# Revit family: SU-420-G_GENERADO
name_source: partatom
category: Equipos mecánicos
revit_build: Autodesk Revit 2014 (Build: 20130308_1515(x64)
units: mm (PartAtom-declared; Revit-internal decimal feet)

## types (14) — shared parameters
Depth = 529 mm  [stored 1.73556 ft]
Fabricante = SAMMIC S.L.
Foodservice Equipment Identifier = Sí
Height = 448 mm  [stored 1.46982 ft]
Revision Code = 1
URL = https://www.sammic.com
URL Cutsheet = http://www.sammic.com
Width = 484 mm  [stored 1.58793 ft]

## per-type parameters (varying)
| type | Comentarios de tipo | Cycle | FL Amps | Modelo | Specification by Manufacturer | Volts | Weight in Pounds |
| Vacuum packing machine SU-416G 230/50-60/1 | Tabletop model. 16 m³/h. 420 mm. | 50 Hz | 4 A | 1140761 | 420 mm. sealing bar.
16 m³/h Busch vacuum pump.
Vacuum controlled by sensor. | 230 V | 143.3 |
| Vacuum packing machine SU-416GP 230/50-60/1 | Tabletop model. 16 m³/h. 420 mm. | 50 Hz | 4 A | 1140763 | 420 mm. sealing bar.
16 m³/h Busch vacuum pump.
Vacuum controlled by sensor. | 230 V | 143.3 |
| Vacuum packing machine SU-416G 120/50-60/1 | Tabletop model. 16 m³/h. 420 mm. | 60 Hz | 8 A | 1140766 | 420 mm. sealing bar.
16 m³/h Busch vacuum pump.
Vacuum controlled by sensor. | 120 V | 143.3 |
| Vacuum packing machine SU-416GP 120/50-60/1 | Tabletop model. 16 m³/h. 420 mm. | 60 Hz | 8 A | 1140768 | 420 mm. sealing bar.
16 m³/h Busch vacuum pump.
Vacuum controlled by sensor. | 120 V | 143.3 |
| Vacuum packing machine SU-416G+ 120/50-60/1 | Tabletop model. 16 m³/h. 420 mm. | 60 Hz | 8 A | 1140769 | 420 mm. sealing bar.
16 m³/h Busch vacuum pump.
Vacuum controlled by sensor. | 120 V | 143.3 |
| Vacuum packing machine SU-416GP+ 120/50-60/1 | Tabletop model. 16 m³/h. 420 mm. | 60 Hz | 8 A | 1140770 | 420 mm. sealing bar.
16 m³/h Busch vacuum pump.
Vacuum controlled by sensor. | 120 V | 143.3 |
| Vacuum packing machine SU-420G 230/50-60/1 | Tabletop model. 20 m³/h. 420 mm. | 50 Hz | 5 A | 1140773 | 420 mm. sealing bar.
20 m³/h Busch vacuum pump.
Vacuum controlled by sensor. | 230 V | 154.3 |
| Vacuum packing machine SU-420GP 230/50-60/1 | Tabletop model. 20 m³/h. 420 mm. | 50 Hz | 5 A | 1140777 | 420 mm. sealing bar.
20 m³/h Busch vacuum pump.
Vacuum controlled by sensor. | 230 V | 154.3 |
| Vacuum packing machine SU-420G+ 230/50-60/1 | Tabletop model. 20 m³/h. 420 mm. | 50 Hz | 5 A | 1140778 | 420 mm. sealing bar.
20 m³/h Busch vacuum pump.
Vacuum controlled by sensor. | 230 V | 154.3 |
| Vacuum packing machine SU-420GP+ 230/50-60/1 | Tabletop model. 20 m³/h. 420 mm. | 50 Hz | 5 A | 1140779 | 420 mm. sealing bar.
20 m³/h Busch vacuum pump.
Vacuum controlled by sensor. | 230 V | 154.3 |
| Vacuum packing machine SU-420G 120/50-60/1 | Tabletop model. 20 m³/h. 420 mm. | 60 Hz | 13 A | 1140782 | 420 mm. sealing bar.
20 m³/h Busch vacuum pump.
Vacuum controlled by sensor. | 120 V | 154.3 |
| Vacuum packing machine SU-420GP 120/50-60/1 | Tabletop model. 20 m³/h. 420 mm. | 60 Hz | 13 A | 1140786 | 420 mm. sealing bar.
20 m³/h Busch vacuum pump.
Vacuum controlled by sensor. | 120 V | 154.3 |
| Vacuum packing machine SU-420G+ 120/50-60/1 | Tabletop model. 20 m³/h. 420 mm. | 60 Hz | 13 A | 1140787 | 420 mm. sealing bar.
20 m³/h Busch vacuum pump.
Vacuum controlled by sensor. | 120 V | 154.3 |
| Vacuum packing machine SU-420GP+ 120/50-60/1 | Tabletop model. 20 m³/h. 420 mm. | 60 Hz | 13 A | 1140788 | 420 mm. sealing bar.
20 m³/h Busch vacuum pump.
Vacuum controlled by sensor. | 120 V | 154.3 |

note: column(s) folded — value = type name in every type: Descripción

note: [stored X ft] marks values corroborated as IEEE doubles in the binary element streams (Revit-internal decimal feet)
